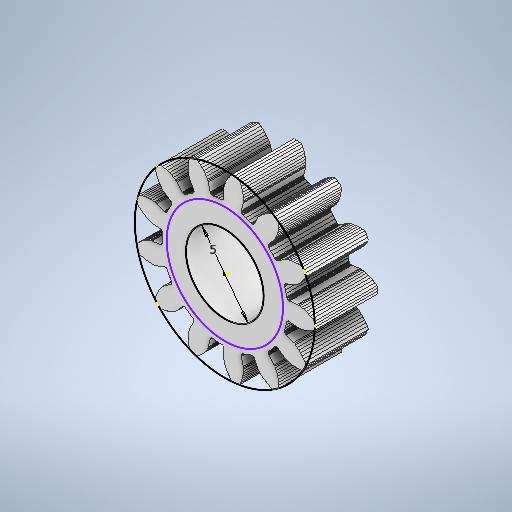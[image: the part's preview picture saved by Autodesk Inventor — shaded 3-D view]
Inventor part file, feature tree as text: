
AUTODESK INVENTOR PART (.ipt)
format: ipt  version: 2025.3 (Build 293356030, 356C)  size: 925,184 bytes
history: native  units: mm
features: extrude x8, sketch x4, other x3
ambient origin geometry x8: Origin, YZ Plane, XZ Plane, XY Plane, X Axis, Y Axis, Z Axis, Center Point
bodies: Body1 (feature_tree)
feature tree (15):
  other  "motor_gear"
  other  "Sólido1"
  other  "MeshFeature1"
  extrude  "Extrusión1"  Depth=3.4mm
  sketch  "Boceto2"  dims[d2=5.0mm d3=4.0mm d4=0.0mm]
  extrude  "Extrusión2"  Depth=4.0mm TaperAngle=0.0deg
  extrude  "Extrusión3"  Depth=10.0mm TaperAngle=0.0deg
  sketch  "Boceto3"  dims[d5=5.0mm d6=10.0mm d7=0.0mm]
  sketch  "Boceto4"  dims[d8=4.015mm d9=0.0mm d12=5.0mm d13=10.0mm d14=0.0mm d15=4.0mm d16=0.0mm d17=5.75mm d18=0.0mm d19=4.0mm d20=0.0mm d21=4.017mm d22=0.0mm]
  extrude  "Extrusión4"  Depth=4.017mm
  extrude  "Extrusión5"  Depth=10.0mm TaperAngle=0.0deg
  extrude  "Extrusión6"  Depth=4.017mm TaperAngle=0.0deg
  extrude  "Extrusión7"  Depth=5.75mm TaperAngle=0.0deg
  extrude  "Extrusión8"  Depth=4.017mm TaperAngle=0.0deg
  sketch  "Boceto1"  dims[d0=6.8mm d1=3.4mm]
